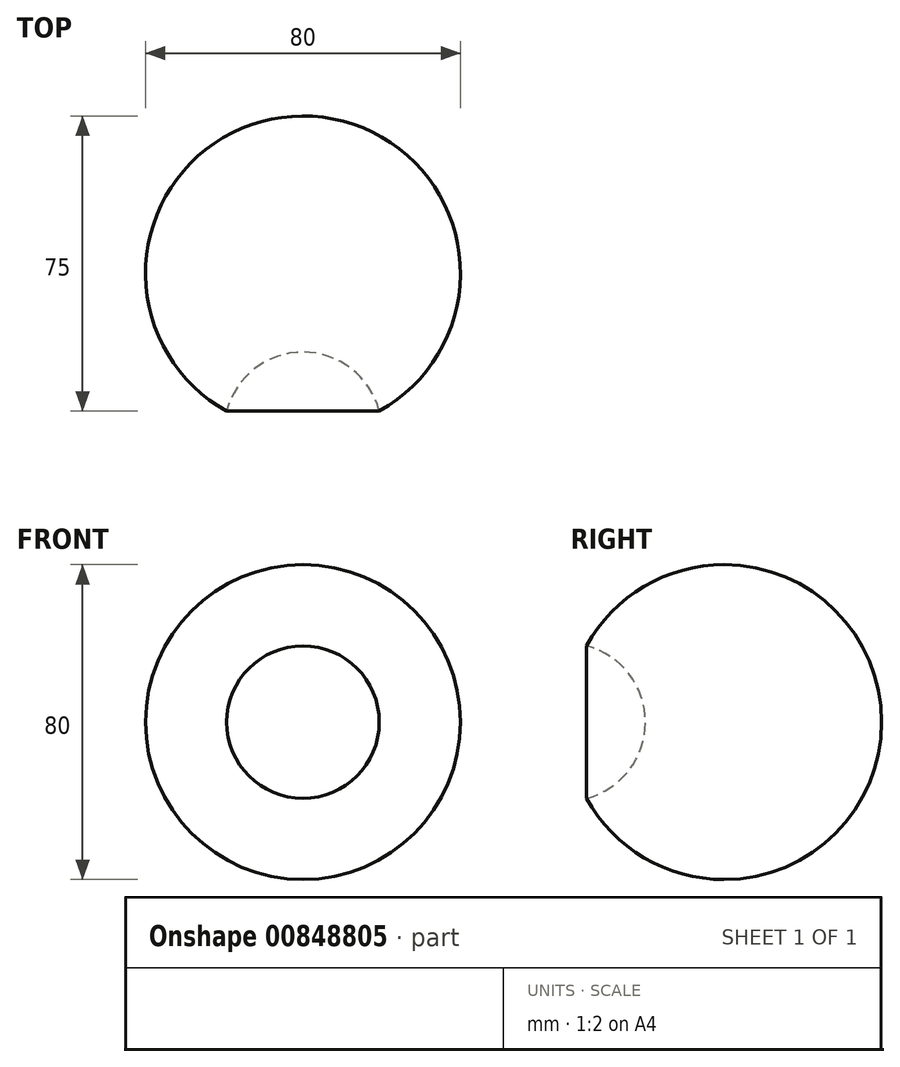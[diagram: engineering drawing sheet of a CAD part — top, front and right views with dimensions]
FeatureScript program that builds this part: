
annotation { "Feature Type Name" : "Feature", "Feature Type Description" : "" }
export const myFeature = defineFeature(function(context is Context, id is Id, definition is map)
    precondition{}
    {
        {
            var Q0;
            Q0=qCreatedBy(makeId("Front.planeOp"),FACE);
            var sketch = newSketch(context, id + "F0", { "sketchPlane" : qUnion([Q0])});
            skLineSegment(sketch, "E0", {"start": v(36.82, 40) * mm, "end": v(-40, 40) * mm, "construction": true});
            skLineSegment(sketch, "E1", {"start": v(-40, 40) * mm, "end": v(-40, -40) * mm, "construction": true});
            skLineSegment(sketch, "E2", {"start": v(-40, -40) * mm, "end": v(0, -40) * mm, "construction": true});
            skArc(sketch, "E3", {"start": v(0, 40) * mm, "mid": v(-40, 0) * mm, "end": v(0, -40) * mm});
            skLineSegment(sketch, "E4", {"start": v(0, 40) * mm, "end": v(0, -40) * mm});
            skSolve(sketch);
        }
        {
            var Q0;
            Q0=makeQuery(id+"F0.imprint","IMPRINT",FACE,{"disambiguationData":[TD([[makeQuery(id+"F0.imprint","IMPRINT",EDGE,{"derivedFrom":sQuery(id+"F0.wireOp",EDGE,"E3")}),1.0]])]});
            var Q1;
            Q1=sQuery(id+"F0.wireOp",EDGE,"E4");
            revolve(context, id + "F1", {"surfaceOperationType" : NewSurfaceOperationType.NEW, "entities" : qUnion([Q0]), "axis" : qUnion([Q1]), "revolveType" : RevolveType.FULL});
        }
        {
            var Q0;
            Q0=qCreatedBy(makeId("Front.planeOp"),FACE);
            cPlane(context, id + "F2", {"entities" : qUnion([Q0]), "cplaneType" : CPlaneType.OFFSET, "offset" : 40 * mm, "width" : 150 * mm, "height" : 150 * mm});
        }
        {
            var Q0;
            Q0=qCreatedBy(id+"F2.planeOp",FACE);
            var sketch = newSketch(context, id + "F3", { "sketchPlane" : qUnion([Q0])});
            skLineSegment(sketch, "E5.bottom", {"start": v(20, 20) * mm, "end": v(-20, 20) * mm, "construction": true});
            skLineSegment(sketch, "E5.top", {"start": v(20, -20) * mm, "end": v(-20, -20) * mm, "construction": true});
            skLineSegment(sketch, "E5.left", {"start": v(20, 20) * mm, "end": v(20, -20) * mm, "construction": true});
            skLineSegment(sketch, "E5.right", {"start": v(-20, 20) * mm, "end": v(-20, -20) * mm, "construction": true});
            skPoint(sketch, "E5.middle", {"position": v(0, 0) * mm});
            skLineSegment(sketch, "E6", {"start": v(0, 20) * mm, "end": v(-20, 20) * mm, "construction": true});
            skLineSegment(sketch, "E7", {"start": v(-20, -20) * mm, "end": v(-20, 20) * mm, "construction": true});
            skArc(sketch, "E8", {"start": v(0, 20) * mm, "mid": v(-20, 0) * mm, "end": v(0, -20) * mm});
            skLineSegment(sketch, "E9", {"start": v(0, 20) * mm, "end": v(0, -20) * mm});
            skSolve(sketch);
        }
        {
            var Q0;
            Q0=makeQuery(id+"F3.imprint","IMPRINT",FACE,{"disambiguationData":[TD([[makeQuery(id+"F3.imprint","IMPRINT",EDGE,{"derivedFrom":sQuery(id+"F3.wireOp",EDGE,"E8")}),1.0]])]});
            var Q1;
            Q1=sQuery(id+"F3.wireOp",EDGE,"E9");
            revolve(context, id + "F4", {"operationType" : NewBodyOperationType.REMOVE, "surfaceOperationType" : NewSurfaceOperationType.NEW, "entities" : qUnion([Q0]), "axis" : qUnion([Q1]), "revolveType" : RevolveType.FULL, "oppositeDirection" : true});
        }
    });
